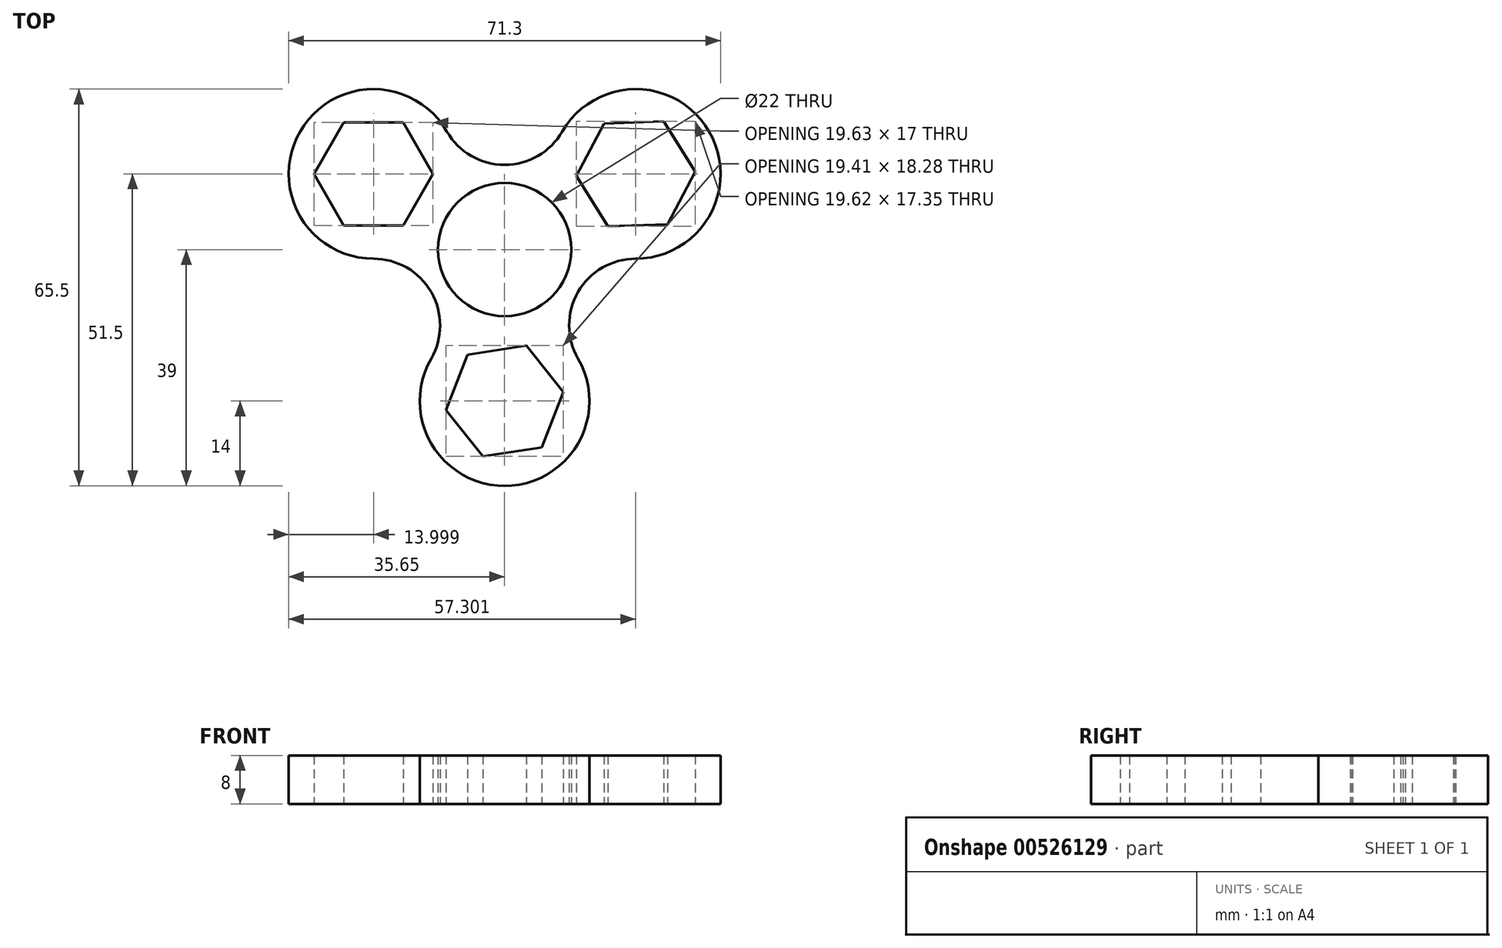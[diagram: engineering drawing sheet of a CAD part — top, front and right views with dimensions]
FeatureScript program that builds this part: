
annotation { "Feature Type Name" : "Feature", "Feature Type Description" : "" }
export const myFeature = defineFeature(function(context is Context, id is Id, definition is map)
    precondition{}
    {
        {
            var Q0;
            Q0=qCreatedBy(makeId("Top.planeOp"),FACE);
            var sketch = newSketch(context, id + "F0", { "sketchPlane" : qUnion([Q0])});
            skArc(sketch, "E0", {"start": v(-9.53, 19.5) * mm, "mid": v(0, 14) * mm, "end": v(9.53, 19.5) * mm});
            skArc(sketch, "E1.2.0", {"start": v(-12.12, -18) * mm, "mid": v(-12.12, -7) * mm, "end": v(-21.65, -1.5) * mm});
            skArc(sketch, "E1.4.0", {"start": v(21.65, -1.5) * mm, "mid": v(12.12, -7) * mm, "end": v(12.12, -18) * mm});
            skPoint(sketch, "E1.center", {"position": v(0, 0) * mm});
            skArc(sketch, "E2.1.0", {"start": v(-9.53, 19.5) * mm, "mid": v(-33.77, 19.5) * mm, "end": v(-21.65, -1.5) * mm});
            skArc(sketch, "E2.3.0", {"start": v(-12.12, -18) * mm, "mid": v(0, -39) * mm, "end": v(12.12, -18) * mm});
            skArc(sketch, "E2.5.0", {"start": v(21.65, -1.5) * mm, "mid": v(33.77, 19.5) * mm, "end": v(9.53, 19.5) * mm});
            skCircle(sketch, "E3", {"center": v(0, 0) * mm, "radius": 11 * mm});
            skCircle(sketch, "E4.cCircle", {"center": v(21.65, 12.5) * mm, "radius": 9.81 * mm, "construction": true});
            skLineSegment(sketch, "E4.0", {"start": v(26.24, 21.17) * mm, "end": v(31.46, 12.86) * mm});
            skLineSegment(sketch, "E4.1", {"start": v(31.46, 12.86) * mm, "end": v(26.87, 4.19) * mm});
            skLineSegment(sketch, "E4.2", {"start": v(26.87, 4.19) * mm, "end": v(17.06, 3.83) * mm});
            skLineSegment(sketch, "E4.3", {"start": v(17.06, 3.83) * mm, "end": v(11.84, 12.14) * mm});
            skLineSegment(sketch, "E4.4", {"start": v(11.84, 12.14) * mm, "end": v(16.44, 20.81) * mm});
            skLineSegment(sketch, "E4.5", {"start": v(16.44, 20.81) * mm, "end": v(26.24, 21.17) * mm});
            skCircle(sketch, "E5.cCircle", {"center": v(0, -25) * mm, "radius": 9.81 * mm, "construction": true});
            skLineSegment(sketch, "E5.0", {"start": v(9.7, -23.52) * mm, "end": v(6.13, -32.66) * mm});
            skLineSegment(sketch, "E5.1", {"start": v(6.13, -32.66) * mm, "end": v(-3.57, -34.14) * mm});
            skLineSegment(sketch, "E5.2", {"start": v(-3.57, -34.14) * mm, "end": v(-9.7, -26.48) * mm});
            skLineSegment(sketch, "E5.3", {"start": v(-9.7, -26.48) * mm, "end": v(-6.13, -17.34) * mm});
            skLineSegment(sketch, "E5.4", {"start": v(-6.13, -17.34) * mm, "end": v(3.57, -15.86) * mm});
            skLineSegment(sketch, "E5.5", {"start": v(3.57, -15.86) * mm, "end": v(9.7, -23.52) * mm});
            skCircle(sketch, "E6.cCircle", {"center": v(-21.65, 12.5) * mm, "radius": 9.81 * mm, "construction": true});
            skLineSegment(sketch, "E6.0", {"start": v(-11.84, 12.5) * mm, "end": v(-16.74, 4) * mm});
            skLineSegment(sketch, "E6.1", {"start": v(-16.74, 4) * mm, "end": v(-26.56, 4) * mm});
            skLineSegment(sketch, "E6.2", {"start": v(-26.56, 4) * mm, "end": v(-31.47, 12.5) * mm});
            skLineSegment(sketch, "E6.3", {"start": v(-31.47, 12.5) * mm, "end": v(-26.56, 21) * mm});
            skLineSegment(sketch, "E6.4", {"start": v(-26.56, 21) * mm, "end": v(-16.74, 21) * mm});
            skLineSegment(sketch, "E6.5", {"start": v(-16.74, 21) * mm, "end": v(-11.84, 12.5) * mm});
            skSolve(sketch);
        }
        {
            var Q0;
            Q0 = qSketchRegion(id + "F0", true);
            extrude(context, id + "F1", {"entities" : qUnion([Q0]), "depth" : 8 * mm, "offsetDistance" : 25 * mm});
        }
    });
